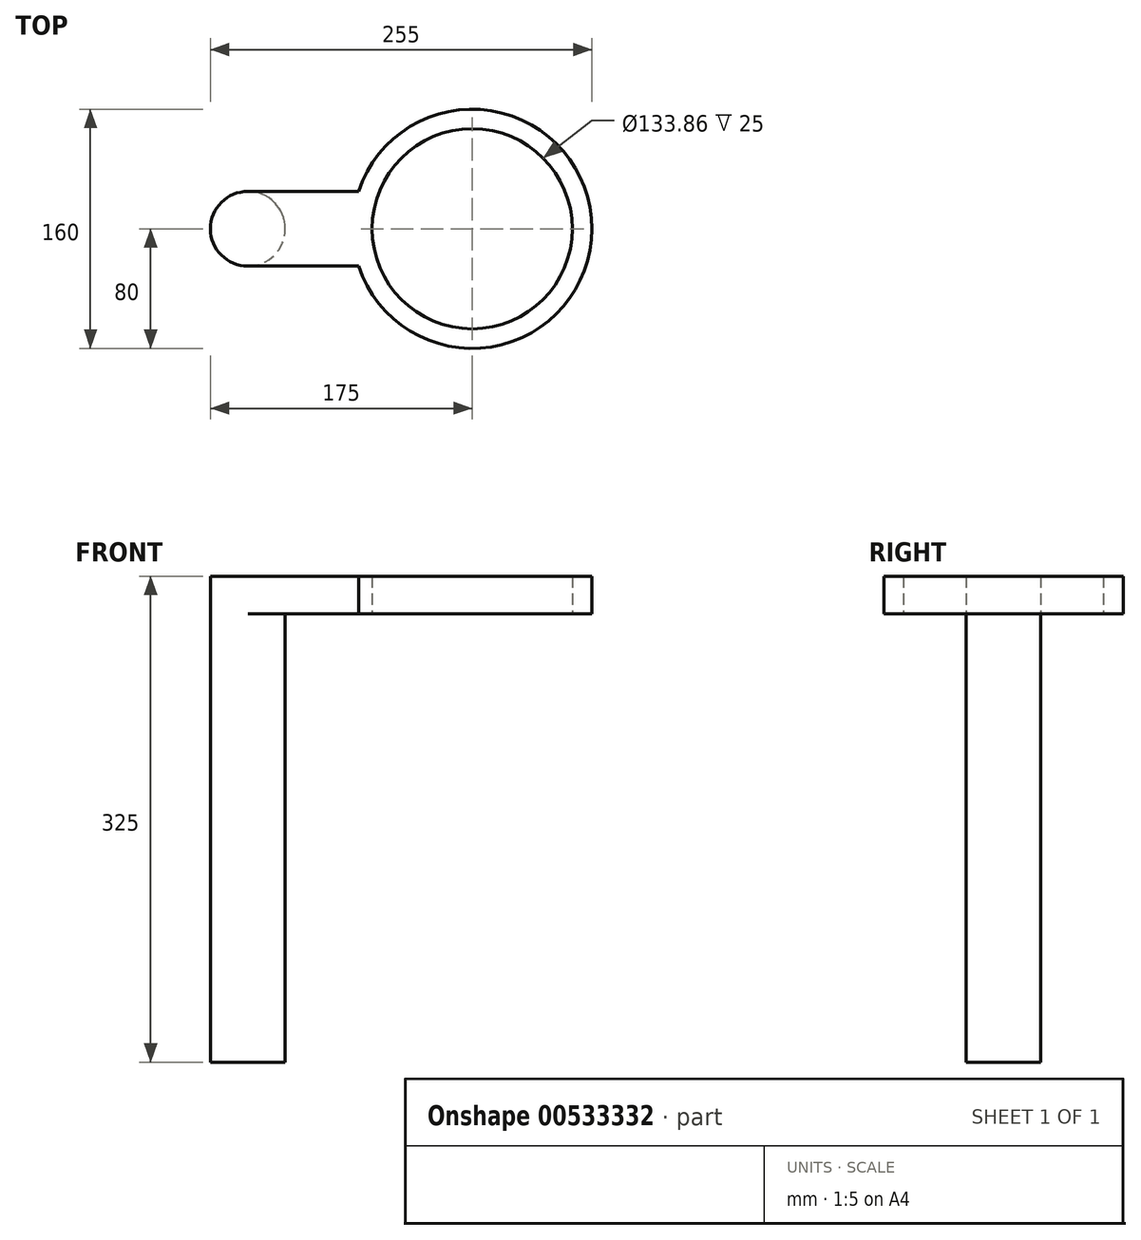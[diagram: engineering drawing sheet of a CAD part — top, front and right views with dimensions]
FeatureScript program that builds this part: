
annotation { "Feature Type Name" : "Feature", "Feature Type Description" : "" }
export const myFeature = defineFeature(function(context is Context, id is Id, definition is map)
    precondition{}
    {
        {
            var Q0;
            Q0=qCreatedBy(makeId("Top.planeOp"),FACE);
            var sketch = newSketch(context, id + "F0", { "sketchPlane" : qUnion([Q0])});
            skCircle(sketch, "E0", {"center": v(0, 0) * mm, "radius": 25 * mm});
            skSolve(sketch);
        }
        {
            var Q0;
            Q0 = qSketchRegion(id + "F0", true);
            extrude(context, id + "F1", {"entities" : qUnion([Q0]), "depth" : 300 * mm, "offsetDistance" : 25 * mm});
        }
        {
            var Q0;
            Q0=makeQuery(id+"F1.opExtrude","CAP_FACE",FACE,{"disambiguationData":[OSD([sQuery(id+"F0.wireOp",EDGE,"E0")])],"isStart":false});
            var sketch = newSketch(context, id + "F2", { "sketchPlane" : qUnion([Q0])});
            skCircle(sketch, "E1", {"center": v(150, 0) * mm, "radius": 80 * mm});
            skLineSegment(sketch, "E2", {"start": v(0, 25) * mm, "end": v(74, 25) * mm});
            skLineSegment(sketch, "E3", {"start": v(0, -25) * mm, "end": v(74, -25) * mm});
            skArc(sketch, "E4", {"start": v(0, 25) * mm, "mid": v(-25, 0) * mm, "end": v(0, -25) * mm});
            skCircle(sketch, "E5", {"center": v(150, 0) * mm, "radius": 66.93 * mm});
            skSolve(sketch);
        }
        {
            var Q0;
            Q0 = qSketchRegion(id + "F2", true);
            extrude(context, id + "F3", {"entities" : qUnion([Q0]), "operationType" : NewBodyOperationType.ADD, "depth" : 25 * mm, "offsetDistance" : 25 * mm});
        }
    });
